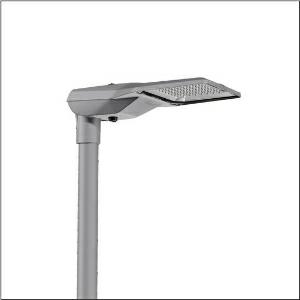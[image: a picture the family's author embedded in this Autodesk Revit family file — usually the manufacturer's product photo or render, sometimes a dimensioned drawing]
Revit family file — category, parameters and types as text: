
# Revit family: streetlight_sl_21_iq_midi___st0_8a_5xe3c31y08nb_292d
name_source: partatom
category: Lighting Fixtures
units: mm (PartAtom-declared; Revit-internal decimal feet)

## family parameters
Cut with Voids When Loaded = No
Host = Face
Light Source = No
Part Type = Normal
Room Calculation Point = No
Round Connector Dimension = Use Diameter
Shared = No

## types (1)
- --- (1 x LED, 21550 lm, 136.6 W, 3000K)
    Apparent Load = 137 VA
    CIE Flux Codes = 41 75 97 100 100
    Color Rendering = 70
    Color Temperature = 3000K
    Default Elevation = 1800 mm
    Description = Streetlight SL 21 iQ midi, mast luminaire, primary light control with lens, of PMMA, primary optical cover: cover, of toughened safety glass, transparent, light distribution: ST0.8a, light emission: direct distribution, primary light characteristic: asymmetric, installation type: post-top, side-entry, LED, High Power LED, rated luminous flux: 21.550lm, luminous efficacy: 158lm/W, light colour: 730, colour temperature: 3000K, control gear: iQ-Street Remote, D4i with power reduction, control: pre-setting: logarithmic dimming characteristic, Street-Remote, Auto-Match, Temp-Guard, Lumen-Switch, Night-Set, Smart-Wire, Light-Fading, Desk-Remote (wireless, voltage-free reading and setting of iQ features in the workshop via application-optimized NFC function/RFID function), optimised constant luminous flux control (CLO 2.0), mains connection: 230..240V, AC, 50/60Hz, start of lifetime: 137W, end of service life: 144W, reduction: 61W, luminaire housing, of diecast aluminium, powder-coated, SITECO metallic grey (DB 702S), corrosivity category C5 high according to DIN EN ISO 12944, please order mast flange separately, inclination adjustable: 0°, 5°, 10°, 15°, sealing non-destructively replaceable, multi-level sealing system, length: 644mm, width: 335mm, height: 110mm, mast flange for spigot size: 42mm (side-entry): 5XC10008XM4, 60/48mm (side-entry/post-top): 5XC10108XM2, 76/60mm (side-entry/post-top): 5XC10108XM1, mounting height: 4..8m, Smart Interface below and above, protection rating (complete): IP66, insulation class (complete): insulation class II (safety insulation), certification: CE, ENEC, ENEC+, VDE, impact resistance: IK10, permissible operating ambient temperature for outdoor applications: -40..+50°C, standard-compliant lighting for roads and squares, packaging unit: 1 piece

Light Distribution: ST0.8a
    Height = 111 mm
    Lamp = 1 x LED
    Lamp Light Flux = 21550 lm
    Lamp Power = 136.6 W
    Lamp count = 1
    Length = 644 mm
    Luminous efficacy = 158 lm/W
    Manufacturer = Siteco
    ModVariant = No
    Model = 5XE3C31Y08NB
    Number of Poles = 1
    OnlyDefault = Yes
    Power Factor = 1
    Product Name = Streetlight SL 21 iQ midi | ST0.8a
    Product group = mast luminaire | pylon top
    ProductGroupID = 6100
    Protection Class = Protection class II
    Protection Degree = IP 66
    RLX_Detail_Level = 1
    RLX_Emergency_Light_Flux = 0 lm
    RLX_Emergency_Type = 0
    RLX_Emergency_Type_DB = No
    RlxData = <blob elided: 91321 chars, md5=ed8e5be3>
    Socket = socket
    Standby Power = 0 W
    System Light Flux = 21550 lm
    System Power = 137 W
    Type Comments = factory setting: luminous flux: 100 % | dim-lin: 254 | 733 mA
    Type Image = l_1004304.jpg
    URL = http://relux.com
    VarID = @adj_113317
    Voltage = 0 V
    Weight = 0.00 kg
    Width = 336 mm

## geometry (parser evidence)
native form markers: Blend x4, Sweep x10
no freeform markers — native parametric forms only
